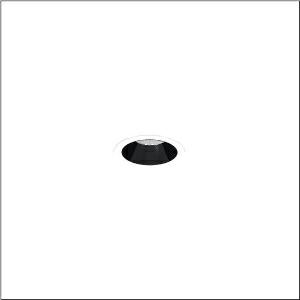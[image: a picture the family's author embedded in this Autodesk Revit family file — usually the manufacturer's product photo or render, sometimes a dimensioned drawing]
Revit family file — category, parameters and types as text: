
# Revit family: lunis_21_s_51db17ea91c
name_source: partatom
category: Lighting Fixtures
units: mm (PartAtom-declared; Revit-internal decimal feet)

## family parameters
Cut with Voids When Loaded = No
Host = Face
Light Source = No
Part Type = Normal
Room Calculation Point = No
Round Connector Dimension = Use Diameter
Shared = No

## types (1)
- --- (1 x LED, 1070 lm, 8 W, 4000K)
    Apparent Load = 8 VA
    CIE Flux Codes = 95 100 100 100 100
    Color Rendering = 80
    Color Temperature = 4000K
    Default Elevation = 1800 mm
    Description = Lunis 21,  S, downlight, light control with lens, of PMMA, anti glare with reflector, of PC, light emission: direct distribution, LED rated luminous flux: 810lm, light colour: 830/840/865, with terminal, 5-pole, mains connection: 220..240V, AC, 50..60Hz, housing, round, of diecast aluminium, traffic white (RAL 9016), diameter: 84mm, clamping range: 1..40mm, protection rating (complete): IP20, protection rating (on room side): IP54, insulation class (complete): insulation class II (safety insulation), certification: CE, impact resistance: IK03, packaging unit: 1 piece
    Height = 0 mm  [stored 0 ft]
    Lamp = 1 x LED
    Lamp Light Flux = 1070 lm
    Lamp Power = 8 W
    Lamp count = 1
    Length = 84 mm
    Luminous efficacy = 134 lm/W
    Manufacturer = Siteco
    ModVariant = No
    Model = 51DB17EA91C
    Mounting Place = Ceiling
    Mounting Type = Recessed
    Number of Poles = 1
    OnlyDefault = Yes
    Power Factor = 1
    Product Name = Lunis 21 S
    Product group = downlight
    ProductGroupID = 400
    Protection Class = Protection class II
    Protection Degree = IP 20
    RLX_Detail_Level = 1
    RLX_Emergency_Light_Flux = 0 lm
    RLX_Emergency_Type = 0
    RLX_Emergency_Type_DB = No
    RlxData = <blob elided: 8805 chars, md5=5876e814>
    Socket = socket
    Standby Power = 0 W
    System Light Flux = 1070 lm
    System Power = 8 W
    Type Comments = individual setting: colour temperature 4000K, luminous flux: 100 % | (OFF | OFF | ON | OFF) | 200 mA
    Type Image = l_1290844.jpg
    URL = http://relux.com
    VarID = @adj_017889
    Voltage = 0 V
    Weight = 0.00 kg
    Width = 0 mm  [stored 0 ft]

note: [stored X ft] marks values corroborated as IEEE doubles in the binary element streams (Revit-internal decimal feet)

## geometry (parser evidence)
native form markers: Sweep x9
no freeform markers — native parametric forms only
